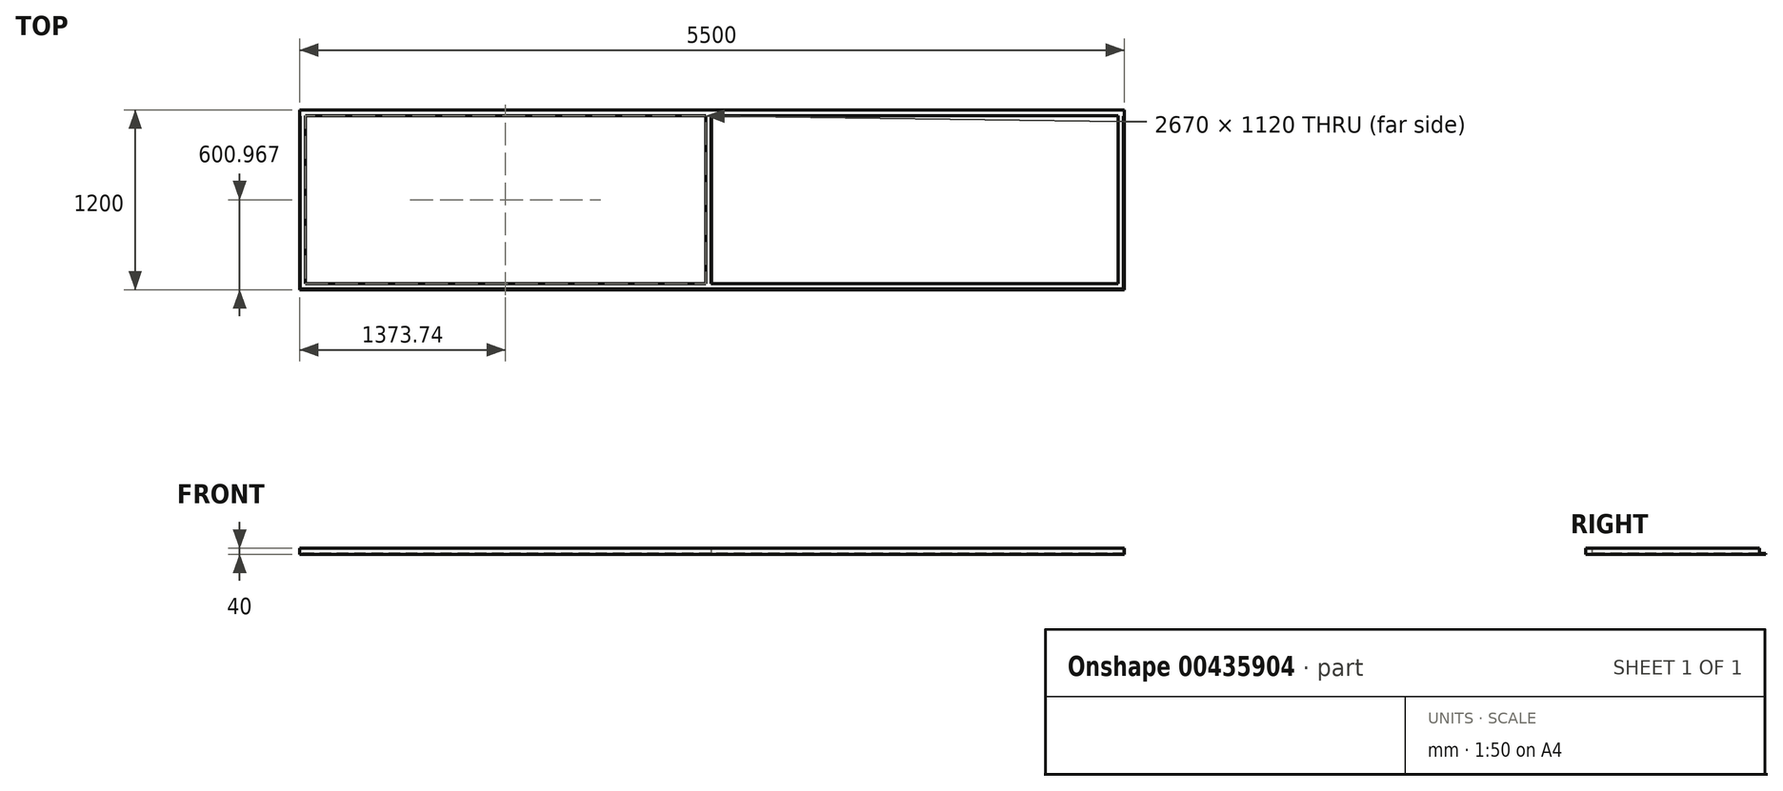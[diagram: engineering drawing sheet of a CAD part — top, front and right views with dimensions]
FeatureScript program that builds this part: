
annotation { "Feature Type Name" : "Feature", "Feature Type Description" : "" }
export const myFeature = defineFeature(function(context is Context, id is Id, definition is map)
    precondition{}
    {
        {
            var Q0;
            Q0=qCreatedBy(makeId("Top.planeOp"),FACE);
            var sketch = newSketch(context, id + "F0", { "sketchPlane" : qUnion([Q0])});
            skLineSegment(sketch, "E0.bottom", {"start": v(2750, -600) * mm, "end": v(-2750, -600) * mm});
            skLineSegment(sketch, "E0.top", {"start": v(2750, 600) * mm, "end": v(-2750, 600) * mm});
            skLineSegment(sketch, "E0.left", {"start": v(2750, -600) * mm, "end": v(2750, 600) * mm});
            skLineSegment(sketch, "E0.right", {"start": v(-2750, -600) * mm, "end": v(-2750, 600) * mm});
            skPoint(sketch, "E0.middle", {"position": v(0, 0) * mm});
            skSolve(sketch);
        }
        {
            var Q0;
            Q0 = qSketchRegion(id + "F0", true);
            extrude(context, id + "F1", {"entities" : qUnion([Q0]), "depth" : 40 * mm});
        }
        {
            var Q0;
            Q0=makeQuery(id+"F1.opExtrude","CAP_FACE",FACE,{"disambiguationData":[OSD([sQuery(id+"F0.wireOp",EDGE,"E0.bottom"),sQuery(id+"F0.wireOp",EDGE,"E0.top"),sQuery(id+"F0.wireOp",EDGE,"E0.left"),sQuery(id+"F0.wireOp",EDGE,"E0.right")])],"isStart":false});
            var sketch = newSketch(context, id + "F2", { "sketchPlane" : qUnion([Q0])});
            skLineSegment(sketch, "E1.bottom", {"start": v(-2745, -595) * mm, "end": v(2745, -595) * mm});
            skLineSegment(sketch, "E1.top", {"start": v(-2745, 595) * mm, "end": v(2745, 595) * mm});
            skLineSegment(sketch, "E1.left", {"start": v(-2745, -595) * mm, "end": v(-2745, 595) * mm});
            skLineSegment(sketch, "E1.right", {"start": v(2745, -595) * mm, "end": v(2745, 595) * mm});
            skPoint(sketch, "E1.middle", {"position": v(0, 0) * mm});
            skSolve(sketch);
        }
        {
            var Q0;
            Q0 = qSketchRegion(id + "F2", true);
            extrude(context, id + "F3", {"entities" : qUnion([Q0]), "operationType" : NewBodyOperationType.REMOVE, "oppositeDirection" : true, "depth" : 35 * mm});
        }
        {
            var Q0;
            Q0=makeQuery(id+"F3.boolean.opBoolean","COPY",FACE,{"derivedFrom":makeQuery(id+"F3.opExtrude","CAP_FACE",FACE,{"disambiguationData":[OSD([sQuery(id+"F2.wireOp",EDGE,"E1.bottom"),sQuery(id+"F2.wireOp",EDGE,"E1.top"),sQuery(id+"F2.wireOp",EDGE,"E1.left"),sQuery(id+"F2.wireOp",EDGE,"E1.right")])],"isStart":false})});
            var sketch = newSketch(context, id + "F4", { "sketchPlane" : qUnion([Q0])});
            skLineSegment(sketch, "E2.bottom", {"start": v(-2711.26, 560.97) * mm, "end": v(-41.26, 560.97) * mm});
            skLineSegment(sketch, "E2.top", {"start": v(-2711.26, -559.03) * mm, "end": v(-41.26, -559.03) * mm});
            skLineSegment(sketch, "E2.left", {"start": v(-2711.26, 560.97) * mm, "end": v(-2711.26, -559.03) * mm});
            skLineSegment(sketch, "E2.right", {"start": v(-41.26, 560.97) * mm, "end": v(-41.26, -559.03) * mm});
            skLineSegment(sketch, "E3.bottom", {"start": v(-1.26, 560.97) * mm, "end": v(2708.74, 560.97) * mm});
            skLineSegment(sketch, "E3.top", {"start": v(-1.26, -559.03) * mm, "end": v(2708.74, -559.03) * mm});
            skLineSegment(sketch, "E3.left", {"start": v(-1.26, 560.97) * mm, "end": v(-1.26, -559.03) * mm});
            skLineSegment(sketch, "E3.right", {"start": v(2708.74, 560.97) * mm, "end": v(2708.74, -559.03) * mm});
            skSolve(sketch);
        }
        {
            var Q0;
            Q0 = qSketchRegion(id + "F4", true);
            extrude(context, id + "F5", {"entities" : qUnion([Q0]), "operationType" : NewBodyOperationType.REMOVE, "oppositeDirection" : true, "depth" : 25 * mm});
        }
        {
            var Q0;
            Q0=makeQuery(id+"F3.boolean.opBoolean","COPY",FACE,{"derivedFrom":makeQuery(id+"F3.opExtrude","CAP_FACE",FACE,{"disambiguationData":[OSD([sQuery(id+"F2.wireOp",EDGE,"E1.bottom"),sQuery(id+"F2.wireOp",EDGE,"E1.top"),sQuery(id+"F2.wireOp",EDGE,"E1.left"),sQuery(id+"F2.wireOp",EDGE,"E1.right")])],"isStart":false})});
            var sketch = newSketch(context, id + "F6", { "sketchPlane" : qUnion([Q0])});
            skLineSegment(sketch, "E4.bottom", {"start": v(-1.26, -559.03) * mm, "end": v(-6.26, -559.03) * mm});
            skLineSegment(sketch, "E4.top", {"start": v(-1.26, 560.97) * mm, "end": v(-6.26, 560.97) * mm});
            skLineSegment(sketch, "E4.left", {"start": v(-1.26, -559.03) * mm, "end": v(-1.26, 560.97) * mm});
            skLineSegment(sketch, "E4.right", {"start": v(-6.26, -559.03) * mm, "end": v(-6.26, 560.97) * mm});
            skSolve(sketch);
        }
        {
            var Q0;
            Q0 = qSketchRegion(id + "F6", true);
            extrude(context, id + "F7", {"entities" : qUnion([Q0]), "operationType" : NewBodyOperationType.ADD, "depth" : 35 * mm});
        }
        {
            var Q0;
            Q0=makeQuery(id+"F1.opExtrude","CAP_FACE",FACE,{"disambiguationData":[OSD([sQuery(id+"F0.wireOp",EDGE,"E0.bottom"),sQuery(id+"F0.wireOp",EDGE,"E0.top"),sQuery(id+"F0.wireOp",EDGE,"E0.left"),sQuery(id+"F0.wireOp",EDGE,"E0.right")])],"isStart":false});
            var sketch = newSketch(context, id + "F8", { "sketchPlane" : qUnion([Q0])});
            skLineSegment(sketch, "E5.bottom", {"start": v(-2750, 637.56) * mm, "end": v(2822.75, 637.56) * mm});
            skLineSegment(sketch, "E5.top", {"start": v(-2750, 559.14) * mm, "end": v(2822.75, 559.14) * mm});
            skLineSegment(sketch, "E5.left", {"start": v(-2750, 637.56) * mm, "end": v(-2750, 559.14) * mm});
            skLineSegment(sketch, "E5.right", {"start": v(2822.75, 637.56) * mm, "end": v(2822.75, 559.14) * mm});
            skSolve(sketch);
        }
        {
            var Q0;
            Q0 = qSketchRegion(id + "F8", true);
            extrude(context, id + "F9", {"entities" : qUnion([Q0]), "operationType" : NewBodyOperationType.REMOVE, "oppositeDirection" : true, "depth" : 35 * mm});
        }
    });
